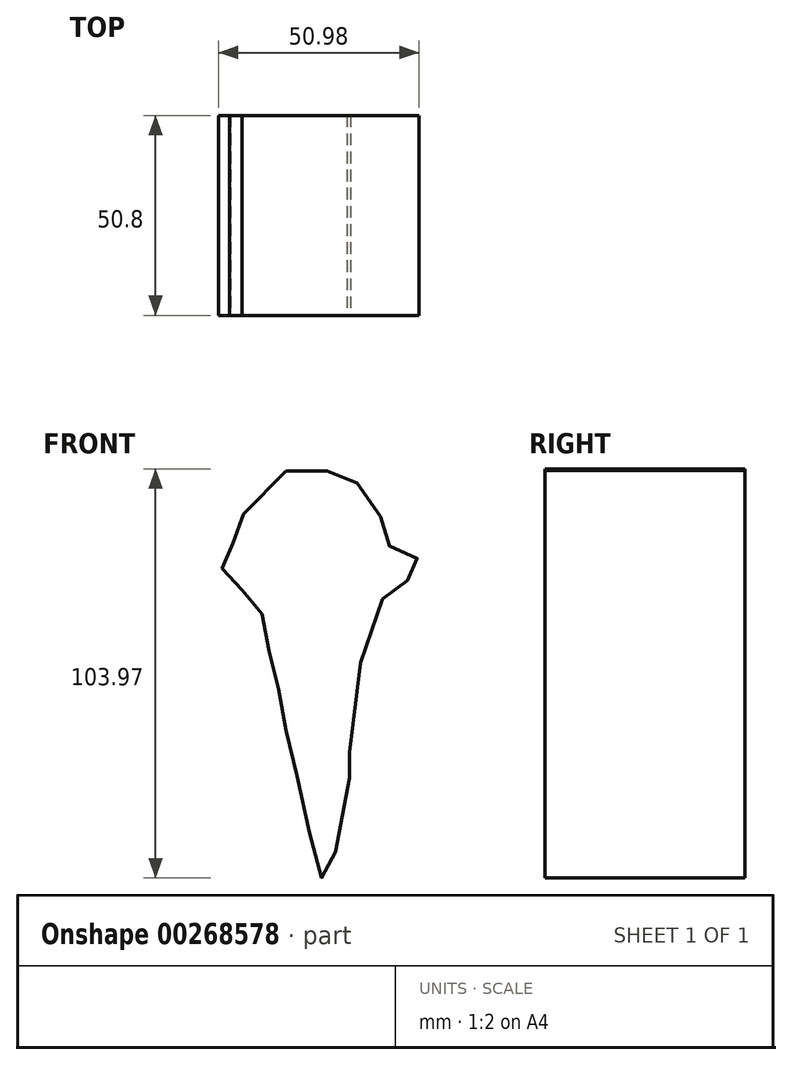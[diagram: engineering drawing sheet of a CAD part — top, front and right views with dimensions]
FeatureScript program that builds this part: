
annotation { "Feature Type Name" : "Feature", "Feature Type Description" : "" }
export const myFeature = defineFeature(function(context is Context, id is Id, definition is map)
    precondition{}
    {
        {
            var Q0;
            Q0=qCreatedBy(makeId("Front.planeOp"),FACE);
            var sketch = newSketch(context, id + "F0", { "sketchPlane" : qUnion([Q0])});
            skFitSpline(sketch, "E0", {"points": [v(-30.67, 43.98) * mm, v(-41.7, 32.3) * mm, v(-42.03, 28.08) * mm, v(-44.95, 24.5) * mm, v(-44.95, 21.58) * mm, v(-47.88, 17.69) * mm, v(-42.68, 14.12) * mm, v(-38.46, 11.52) * mm, v(-36.52, 6.33) * mm, v(-35.54, 0) * mm, v(-33.27, -7.3) * mm, v(-32.3, -13.8) * mm, v(-30.67, -22.23) * mm, v(-28.4, -31.97) * mm, v(-24.83, -46.58) * mm, v(-22.56, -58.84) * mm, v(-19.31, -58.84) * mm, v(-18.01, -51.77) * mm, v(-14.44, -31) * mm, v(-15.1, -30.35) * mm, v(-14.12, -25.16) * mm, v(-7.95, 10.55) * mm, v(-3.4, 11.85) * mm, v(0, 16.07) * mm, v(2.76, 18.66) * mm, v(2.76, 21.58) * mm, v(0, 23.86) * mm, v(-4.7, 25.16) * mm, v(-5.36, 28.4) * mm, v(-7.95, 34.57) * mm, v(-12.5, 40.74) * mm, v(-16.72, 43.98) * mm, v(-22.56, 43.98) * mm, v(-30.67, 43.98) * mm]});
            skSolve(sketch);
        }
        {
            var Q0;
            Q0=makeQuery(id+"F0.imprint","IMPRINT",FACE,{"disambiguationData":[TD([[makeQuery(id+"F0.imprint","IMPRINT",EDGE,{"derivedFrom":sQuery(id+"F0.wireOp",EDGE,"E0")}),1.0]])]});
            extrude(context, id + "F1", {"entities" : qUnion([Q0]), "oppositeDirection" : true, "depth" : 50.8 * mm});
        }
    });
